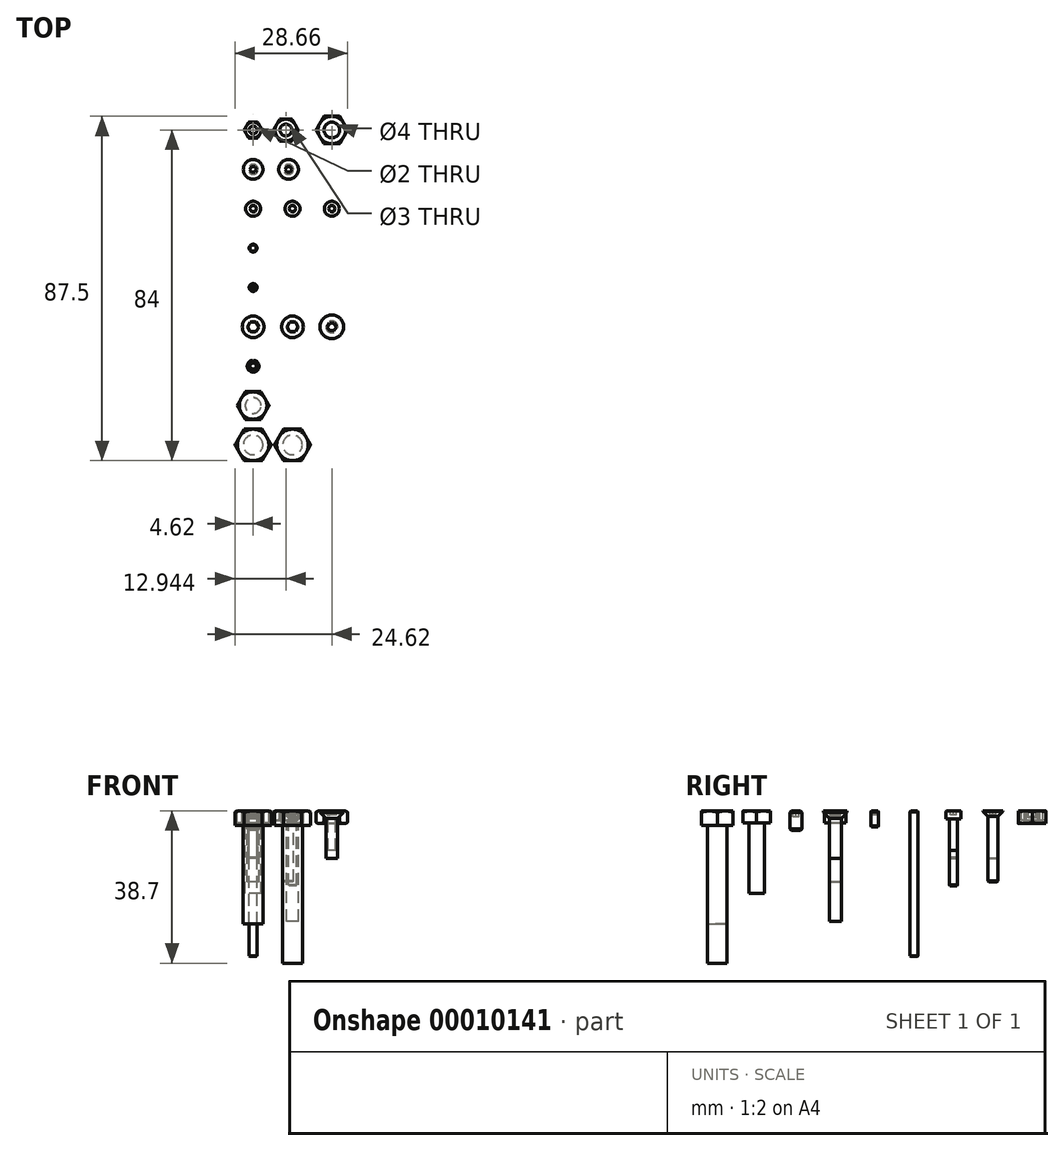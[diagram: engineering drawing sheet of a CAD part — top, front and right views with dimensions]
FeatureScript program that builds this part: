
annotation { "Feature Type Name" : "Feature", "Feature Type Description" : "" }
export const myFeature = defineFeature(function(context is Context, id is Id, definition is map)
    precondition{}
    {
        {
            var Q0;
            Q0=qCreatedBy(makeId("Top.planeOp"),FACE);
            var sketch = newSketch(context, id + "F0", { "sketchPlane" : qUnion([Q0])});
            skCircle(sketch, "E0.cCircle", {"center": v(0, 0) * mm, "radius": 2 * mm, "construction": true});
            skLineSegment(sketch, "E0.0", {"start": v(1.15, -2) * mm, "end": v(-1.15, -2) * mm});
            skLineSegment(sketch, "E0.1", {"start": v(-1.15, -2) * mm, "end": v(-2.3, 0) * mm});
            skLineSegment(sketch, "E0.2", {"start": v(-2.3, 0) * mm, "end": v(-1.15, 2) * mm});
            skLineSegment(sketch, "E0.3", {"start": v(-1.15, 2) * mm, "end": v(1.15, 2) * mm});
            skLineSegment(sketch, "E0.4", {"start": v(1.15, 2) * mm, "end": v(2.3, 0) * mm});
            skLineSegment(sketch, "E0.5", {"start": v(2.3, 0) * mm, "end": v(1.15, -2) * mm});
            skPoint(sketch, "E0.0.midPoint", {"position": v(0, -2) * mm});
            skCircle(sketch, "E1", {"center": v(0, 0) * mm, "radius": 1 * mm});
            skCircle(sketch, "E2", {"center": v(0, 0) * mm, "radius": 2 * mm});
            skSolve(sketch);
        }
        {
            var Q0;
            {var subQ1=sQuery(id+"F0.wireOp",EDGE,"E0.3");var subQ3=sQuery(id+"F0.wireOp",EDGE,"E0.2");var subQ5=makeQuery(id+"F0.imprint","INTERSECT",VERTEX,{"derivedFrom":[subQ3,subQ1]});Q0=makeQuery(id+"F0.imprint","IMPRINT",FACE,{"disambiguationData":[TD([[makeQuery(id+"F0.imprint","IMPRINT",EDGE,{"disambiguationData":[TD([[subQ5,1.0]])],"derivedFrom":subQ3}),-1.0]])]});}
            var Q1;
            {var subQ1=sQuery(id+"F0.wireOp",EDGE,"E0.2");var subQ3=sQuery(id+"F0.wireOp",EDGE,"E0.1");var subQ5=makeQuery(id+"F0.imprint","INTERSECT",VERTEX,{"derivedFrom":[subQ3,subQ1]});Q1=makeQuery(id+"F0.imprint","IMPRINT",FACE,{"disambiguationData":[TD([[makeQuery(id+"F0.imprint","IMPRINT",EDGE,{"disambiguationData":[TD([[subQ5,1.0]])],"derivedFrom":subQ3}),-1.0]])]});}
            var Q2;
            Q2=makeQuery(id+"F0.imprint","IMPRINT",FACE,{"disambiguationData":[TD([[makeQuery(id+"F0.imprint","IMPRINT",EDGE,{"derivedFrom":sQuery(id+"F0.wireOp",EDGE,"E1")}),-1.0]])]});
            var Q3;
            {var subQ1=sQuery(id+"F0.wireOp",EDGE,"E0.4");var subQ3=sQuery(id+"F0.wireOp",EDGE,"E0.3");var subQ5=makeQuery(id+"F0.imprint","INTERSECT",VERTEX,{"derivedFrom":[subQ3,subQ1]});Q3=makeQuery(id+"F0.imprint","IMPRINT",FACE,{"disambiguationData":[TD([[makeQuery(id+"F0.imprint","IMPRINT",EDGE,{"disambiguationData":[TD([[subQ5,1.0]])],"derivedFrom":subQ3}),-1.0]])]});}
            var Q4;
            {var subQ1=sQuery(id+"F0.wireOp",EDGE,"E0.5");var subQ3=sQuery(id+"F0.wireOp",EDGE,"E0.4");var subQ5=makeQuery(id+"F0.imprint","INTERSECT",VERTEX,{"derivedFrom":[subQ3,subQ1]});Q4=makeQuery(id+"F0.imprint","IMPRINT",FACE,{"disambiguationData":[TD([[makeQuery(id+"F0.imprint","IMPRINT",EDGE,{"disambiguationData":[TD([[subQ5,1.0]])],"derivedFrom":subQ3}),-1.0]])]});}
            var Q5;
            {var subQ1=sQuery(id+"F0.wireOp",EDGE,"E0.5");var subQ3=sQuery(id+"F0.wireOp",EDGE,"E0.0");var subQ5=makeQuery(id+"F0.imprint","INTERSECT",VERTEX,{"derivedFrom":[subQ3,subQ1]});Q5=makeQuery(id+"F0.imprint","IMPRINT",FACE,{"disambiguationData":[TD([[makeQuery(id+"F0.imprint","IMPRINT",EDGE,{"disambiguationData":[TD([[subQ5,-1.0]])],"derivedFrom":subQ3}),-1.0]])]});}
            var Q6;
            {var subQ1=sQuery(id+"F0.wireOp",EDGE,"E0.1");var subQ3=sQuery(id+"F0.wireOp",EDGE,"E0.0");var subQ5=makeQuery(id+"F0.imprint","INTERSECT",VERTEX,{"derivedFrom":[subQ3,subQ1]});Q6=makeQuery(id+"F0.imprint","IMPRINT",FACE,{"disambiguationData":[TD([[makeQuery(id+"F0.imprint","IMPRINT",EDGE,{"disambiguationData":[TD([[subQ5,1.0]])],"derivedFrom":subQ3}),-1.0]])]});}
            extrude(context, id + "F1", {"entities" : qUnion([Q0, Q1, Q2, Q3, Q4, Q5, Q6]), "oppositeDirection" : true, "depth" : 1.6 * mm});
        }
        {
            var Q0;
            Q0=qCreatedBy(makeId("Front.planeOp"),FACE);
            var sketch = newSketch(context, id + "F2", { "sketchPlane" : qUnion([Q0])});
            skLineSegment(sketch, "E3.0", {"start": v(-2, 0) * mm, "end": v(2, 0) * mm});
            skLineSegment(sketch, "E3.1", {"start": v(2.3, -1.6) * mm, "end": v(2.3, 0) * mm});
            skLineSegment(sketch, "E3.2", {"start": v(-2.3, -1.6) * mm, "end": v(-2.3, 0) * mm});
            skLineSegment(sketch, "E4", {"start": v(2, 0) * mm, "end": v(2.3, -0.18) * mm});
            skLineSegment(sketch, "E5", {"start": v(2, 0) * mm, "end": v(2.3, 0) * mm});
            skLineSegment(sketch, "E6", {"start": v(0, 0) * mm, "end": v(0, -1.88) * mm, "construction": true});
            skLineSegment(sketch, "E7", {"start": v(-2.3, -0.8) * mm, "end": v(0, -0.8) * mm, "construction": true});
            skLineSegment(sketch, "E8.0.MirrorCS", {"start": v(2, -1.6) * mm, "end": v(2.3, -1.6) * mm});
            skLineSegment(sketch, "E9.0.MirrorCS", {"start": v(2.3, 0) * mm, "end": v(2.3, -1.6) * mm});
            skLineSegment(sketch, "E10.0.MirrorCS", {"start": v(2, -1.6) * mm, "end": v(2.3, -1.42) * mm});
            skSolve(sketch);
        }
        {
            var Q0;
            {var subQ2=sQuery(id+"F2.wireOp",EDGE,"E4");Q0=makeQuery(id+"F2.imprint","IMPRINT",FACE,{"disambiguationData":[TD([[makeQuery(id+"F2.imprint","IMPRINT",EDGE,{"derivedFrom":subQ2}),1.0]])]});}
            var Q1;
            {var subQ2=sQuery(id+"F2.wireOp",EDGE,"E8.0.MirrorCS");Q1=makeQuery(id+"F2.imprint","IMPRINT",FACE,{"disambiguationData":[TD([[makeQuery(id+"F2.imprint","IMPRINT",EDGE,{"derivedFrom":subQ2}),1.0]])]});}
            var Q2;
            Q2=sQuery(id+"F2.wireOp",EDGE,"E6");
            revolve(context, id + "F3", {"operationType" : NewBodyOperationType.REMOVE, "entities" : qUnion([Q0, Q1]), "axis" : qUnion([Q2]), "revolveType" : RevolveType.FULL, "oppositeDirection" : true});
        }
        {
            var Q0;
            Q0=qCreatedBy(makeId("Top.planeOp"),FACE);
            var sketch = newSketch(context, id + "F4", { "sketchPlane" : qUnion([Q0])});
            skCircle(sketch, "E11.cCircle", {"center": v(8.32, 0) * mm, "radius": 2.75 * mm, "construction": true});
            skLineSegment(sketch, "E11.0", {"start": v(9.91, -2.75) * mm, "end": v(6.74, -2.75) * mm});
            skLineSegment(sketch, "E11.1", {"start": v(6.74, -2.75) * mm, "end": v(5.15, 0) * mm});
            skLineSegment(sketch, "E11.2", {"start": v(5.15, 0) * mm, "end": v(6.74, 2.75) * mm});
            skLineSegment(sketch, "E11.3", {"start": v(6.74, 2.75) * mm, "end": v(9.91, 2.75) * mm});
            skLineSegment(sketch, "E11.4", {"start": v(9.91, 2.75) * mm, "end": v(11.5, 0) * mm});
            skLineSegment(sketch, "E11.5", {"start": v(11.5, 0) * mm, "end": v(9.91, -2.75) * mm});
            skPoint(sketch, "E11.0.midPoint", {"position": v(8.32, -2.75) * mm});
            skCircle(sketch, "E12", {"center": v(8.32, 0) * mm, "radius": 1.5 * mm});
            skSolve(sketch);
        }
        {
            var Q0;
            Q0=makeQuery(id+"F4.imprint","IMPRINT",FACE,{"disambiguationData":[TD([[makeQuery(id+"F4.imprint","IMPRINT",EDGE,{"derivedFrom":sQuery(id+"F4.wireOp",EDGE,"E11.0")}),-1.0]])]});
            extrude(context, id + "F5", {"entities" : qUnion([Q0]), "oppositeDirection" : true, "depth" : 2.4 * mm});
        }
        {
            var Q0;
            Q0=qCreatedBy(makeId("Front.planeOp"),FACE);
            var sketch = newSketch(context, id + "F6", { "sketchPlane" : qUnion([Q0])});
            skLineSegment(sketch, "E13.0", {"start": v(5.57, 0) * mm, "end": v(11.07, 0) * mm});
            skLineSegment(sketch, "E13.1", {"start": v(5.15, -2.4) * mm, "end": v(5.15, 0) * mm});
            skLineSegment(sketch, "E13.2", {"start": v(11.5, -2.4) * mm, "end": v(11.5, 0) * mm});
            skLineSegment(sketch, "E14", {"start": v(5.57, 0) * mm, "end": v(5.15, -0.25) * mm});
            skLineSegment(sketch, "E15", {"start": v(5.57, 0) * mm, "end": v(5.15, 0) * mm});
            skLineSegment(sketch, "E16", {"start": v(8.32, 0) * mm, "end": v(8.32, -2.47) * mm, "construction": true});
            skLineSegment(sketch, "E17", {"start": v(11.5, -1.2) * mm, "end": v(8.32, -1.2) * mm, "construction": true});
            skLineSegment(sketch, "E18.0.MirrorCS", {"start": v(5.57, -2.4) * mm, "end": v(5.15, -2.15) * mm});
            skLineSegment(sketch, "E19.0.MirrorCS", {"start": v(5.15, 0) * mm, "end": v(5.15, -2.4) * mm});
            skLineSegment(sketch, "E20.0.MirrorCS", {"start": v(5.57, -2.4) * mm, "end": v(5.15, -2.4) * mm});
            skSolve(sketch);
        }
        {
            var Q0;
            {var subQ2=sQuery(id+"F6.wireOp",EDGE,"E14");Q0=makeQuery(id+"F6.imprint","IMPRINT",FACE,{"disambiguationData":[TD([[makeQuery(id+"F6.imprint","IMPRINT",EDGE,{"derivedFrom":subQ2}),-1.0]])]});}
            var Q1;
            {var subQ2=sQuery(id+"F6.wireOp",EDGE,"E18.0.MirrorCS");Q1=makeQuery(id+"F6.imprint","IMPRINT",FACE,{"disambiguationData":[TD([[makeQuery(id+"F6.imprint","IMPRINT",EDGE,{"derivedFrom":subQ2}),1.0]])]});}
            var Q2;
            Q2=sQuery(id+"F6.wireOp",EDGE,"E16");
            revolve(context, id + "F7", {"operationType" : NewBodyOperationType.REMOVE, "entities" : qUnion([Q0, Q1]), "axis" : qUnion([Q2]), "revolveType" : RevolveType.FULL, "oppositeDirection" : true});
        }
        {
            var Q0;
            Q0=qCreatedBy(makeId("Top.planeOp"),FACE);
            var sketch = newSketch(context, id + "F8", { "sketchPlane" : qUnion([Q0])});
            skCircle(sketch, "E21", {"center": v(17, 0) * mm, "radius": 2.5 * mm});
            skCircle(sketch, "E22", {"center": v(17, 0) * mm, "radius": 1.25 * mm});
            skCircle(sketch, "E23.cCircle", {"center": v(17, 0) * mm, "radius": 0.75 * mm, "construction": true});
            skLineSegment(sketch, "E23.0", {"start": v(17.43, -0.75) * mm, "end": v(16.57, -0.75) * mm});
            skLineSegment(sketch, "E23.1", {"start": v(16.57, -0.75) * mm, "end": v(16.13, 0) * mm});
            skLineSegment(sketch, "E23.2", {"start": v(16.13, 0) * mm, "end": v(16.57, 0.75) * mm});
            skLineSegment(sketch, "E23.3", {"start": v(16.57, 0.75) * mm, "end": v(17.43, 0.75) * mm});
            skLineSegment(sketch, "E23.4", {"start": v(17.43, 0.75) * mm, "end": v(17.87, 0) * mm});
            skLineSegment(sketch, "E23.5", {"start": v(17.87, 0) * mm, "end": v(17.43, -0.75) * mm});
            skPoint(sketch, "E23.0.midPoint", {"position": v(17, -0.75) * mm});
            skSolve(sketch);
        }
        {
            var Q0;
            Q0=makeQuery(id+"F8.imprint","IMPRINT",FACE,{"disambiguationData":[TD([[makeQuery(id+"F8.imprint","IMPRINT",EDGE,{"derivedFrom":sQuery(id+"F8.wireOp",EDGE,"E22")}),1.0]])]});
            var Q1;
            Q1=makeQuery(id+"F8.imprint","IMPRINT",FACE,{"disambiguationData":[TD([[makeQuery(id+"F8.imprint","IMPRINT",EDGE,{"derivedFrom":sQuery(id+"F8.wireOp",EDGE,"E23.0")}),-1.0]])]});
            extrude(context, id + "F9", {"entities" : qUnion([Q0, Q1]), "oppositeDirection" : true, "depth" : 15 * mm});
        }
        {
            var Q0;
            Q0=makeQuery(id+"F8.imprint","IMPRINT",FACE,{"disambiguationData":[TD([[makeQuery(id+"F8.imprint","IMPRINT",EDGE,{"derivedFrom":sQuery(id+"F8.wireOp",EDGE,"E21")}),1.0]])]});
            extrude(context, id + "F10", {"entities" : qUnion([Q0]), "operationType" : NewBodyOperationType.ADD, "oppositeDirection" : true, "depth" : 1.5 * mm});
        }
        {
            var Q0;
            Q0=makeQuery(id+"F10.opExtrude","CAP_EDGE",EDGE,{"disambiguationData":[OSD([sQuery(id+"F8.wireOp",EDGE,"E21")])],"isStart":false});
            chamfer(context, id + "F11", {"entities" : qUnion([Q0]), "width" : 1.4 * mm, "tangentPropagation" : true});
        }
        {
            var Q0;
            Q0=makeQuery(id+"F8.imprint","IMPRINT",FACE,{"disambiguationData":[TD([[makeQuery(id+"F8.imprint","IMPRINT",EDGE,{"derivedFrom":sQuery(id+"F8.wireOp",EDGE,"E23.0")}),-1.0]])]});
            extrude(context, id + "F12", {"entities" : qUnion([Q0]), "operationType" : NewBodyOperationType.REMOVE, "oppositeDirection" : true, "depth" : 1 * mm});
        }
        {
            var Q0;
            Q0=makeQuery(id+"F9.opExtrude","SWEPT_BODY",BODY,{"disambiguationData":[OSD([sQuery(id+"F8.wireOp",EDGE,"E22")])]});
            transform(context, id + "F13", {"entities" : qUnion([Q0]), "transformType" : TransformType.TRANSLATION_3D, "dx" : 10 * mm, "dy" : 0 * mm, "dz" : 0 * mm, "makeCopy" : true});
        }
        {
            var Q0;
            Q0=makeQuery(id+"F13.opPattern","COPY",FACE,{"derivedFrom":makeQuery(id+"F9.opExtrude","CAP_FACE",FACE,{"disambiguationData":[OSD([sQuery(id+"F8.wireOp",EDGE,"E22")])],"isStart":false}),"instanceName":"1"});
            extrude(context, id + "F14", {"entities" : qUnion([Q0]), "operationType" : NewBodyOperationType.ADD, "depth" : 3 * mm});
        }
        {
            var Q0;
            Q0=makeQuery(id+"F9.opExtrude","SWEPT_BODY",BODY,{"disambiguationData":[OSD([sQuery(id+"F8.wireOp",EDGE,"E22")])]});
            transform(context, id + "F15", {"entities" : qUnion([Q0]), "transformType" : TransformType.TRANSLATION_3D, "dx" : -(17 * mm), "dy" : -(10 * mm), "dz" : 0 * mm, "makeCopy" : false});
        }
        {
            var Q0;
            Q0=makeQuery(id+"F13.opPattern","COPY",BODY,{"derivedFrom":makeQuery(id+"F9.opExtrude","SWEPT_BODY",BODY,{"disambiguationData":[OSD([sQuery(id+"F8.wireOp",EDGE,"E22")])]}),"instanceName":"1"});
            transform(context, id + "F16", {"entities" : qUnion([Q0]), "transformType" : TransformType.TRANSLATION_3D, "dx" : -(18 * mm), "dy" : -10 * mm, "dz" : 0 * mm, "makeCopy" : false});
        }
        {
            var Q0;
            Q0=qCreatedBy(makeId("Top.planeOp"),FACE);
            var sketch = newSketch(context, id + "F17", { "sketchPlane" : qUnion([Q0])});
            skCircle(sketch, "E24", {"center": v(0, -20) * mm, "radius": 1.9 * mm});
            skCircle(sketch, "E25", {"center": v(0, -20) * mm, "radius": 1 * mm});
            skCircle(sketch, "E26.cCircle", {"center": v(0, -20) * mm, "radius": 0.75 * mm, "construction": true});
            skLineSegment(sketch, "E26.0", {"start": v(0.43, -20.75) * mm, "end": v(-0.43, -20.75) * mm});
            skLineSegment(sketch, "E26.1", {"start": v(-0.43, -20.75) * mm, "end": v(-0.87, -20) * mm});
            skLineSegment(sketch, "E26.2", {"start": v(-0.87, -20) * mm, "end": v(-0.43, -19.25) * mm});
            skLineSegment(sketch, "E26.3", {"start": v(-0.43, -19.25) * mm, "end": v(0.43, -19.25) * mm});
            skLineSegment(sketch, "E26.4", {"start": v(0.43, -19.25) * mm, "end": v(0.87, -20) * mm});
            skLineSegment(sketch, "E26.5", {"start": v(0.87, -20) * mm, "end": v(0.43, -20.75) * mm});
            skPoint(sketch, "E26.0.midPoint", {"position": v(0, -20.75) * mm});
            skSolve(sketch);
        }
        {
            var Q0;
            Q0=makeQuery(id+"F17.imprint","IMPRINT",FACE,{"disambiguationData":[TD([[makeQuery(id+"F17.imprint","IMPRINT",EDGE,{"derivedFrom":sQuery(id+"F17.wireOp",EDGE,"E25")}),1.0]])]});
            var Q1;
            Q1=makeQuery(id+"F17.imprint","IMPRINT",FACE,{"disambiguationData":[TD([[makeQuery(id+"F17.imprint","IMPRINT",EDGE,{"derivedFrom":sQuery(id+"F17.wireOp",EDGE,"E26.0")}),-1.0]])]});
            extrude(context, id + "F18", {"entities" : qUnion([Q0, Q1]), "oppositeDirection" : true, "depth" : 12 * mm});
        }
        {
            var Q0;
            Q0=makeQuery(id+"F17.imprint","IMPRINT",FACE,{"disambiguationData":[TD([[makeQuery(id+"F17.imprint","IMPRINT",EDGE,{"derivedFrom":sQuery(id+"F17.wireOp",EDGE,"E24")}),1.0]])]});
            extrude(context, id + "F19", {"entities" : qUnion([Q0]), "operationType" : NewBodyOperationType.ADD, "oppositeDirection" : true, "depth" : 2 * mm});
        }
        {
            var Q0;
            Q0=makeQuery(id+"F17.imprint","IMPRINT",FACE,{"disambiguationData":[TD([[makeQuery(id+"F17.imprint","IMPRINT",EDGE,{"derivedFrom":sQuery(id+"F17.wireOp",EDGE,"E26.0")}),-1.0]])]});
            extrude(context, id + "F20", {"entities" : qUnion([Q0]), "operationType" : NewBodyOperationType.REMOVE, "oppositeDirection" : true, "depth" : 1 * mm});
        }
        {
            var Q0;
            Q0=makeQuery(id+"F19.opExtrude","CAP_EDGE",EDGE,{"disambiguationData":[OSD([sQuery(id+"F17.wireOp",EDGE,"E24")])],"isStart":true});
            fillet(context, id + "F21", {"entities" : qUnion([Q0]), "radius" : 0.2 * mm, "tangentPropagation" : true, "allowEdgeOverflow" : false});
        }
        {
            var Q0;
            Q0=makeQuery(id+"F18.opExtrude","SWEPT_BODY",BODY,{"disambiguationData":[OSD([sQuery(id+"F17.wireOp",EDGE,"E25")])]});
            transform(context, id + "F22", {"entities" : qUnion([Q0]), "transformType" : TransformType.TRANSLATION_3D, "dx" : 10 * mm, "dy" : 0 * mm, "dz" : 0 * mm, "makeCopy" : true});
        }
        {
            var Q0;
            Q0=makeQuery(id+"F22.opPattern","COPY",FACE,{"derivedFrom":makeQuery(id+"F18.opExtrude","CAP_FACE",FACE,{"disambiguationData":[OSD([sQuery(id+"F17.wireOp",EDGE,"E25")])],"isStart":false}),"instanceName":"1"});
            extrude(context, id + "F23", {"entities" : qUnion([Q0]), "operationType" : NewBodyOperationType.ADD, "depth" : 7 * mm});
        }
        {
            var Q0;
            Q0=qCreatedBy(makeId("Top.planeOp"),FACE);
            var sketch = newSketch(context, id + "F24", { "sketchPlane" : qUnion([Q0])});
            skCircle(sketch, "E27", {"center": v(0, -30) * mm, "radius": 1 * mm});
            skSolve(sketch);
        }
        {
            var Q0;
            Q0=makeQuery(id+"F24.imprint","IMPRINT",FACE,{"disambiguationData":[TD([[makeQuery(id+"F24.imprint","IMPRINT",EDGE,{"derivedFrom":sQuery(id+"F24.wireOp",EDGE,"E27")}),1.0]])]});
            extrude(context, id + "F25", {"entities" : qUnion([Q0]), "oppositeDirection" : true, "depth" : 37 * mm});
        }
        {
            var Q0;
            Q0=makeQuery(id+"F25.opExtrude","CAP_EDGE",EDGE,{"disambiguationData":[OSD([sQuery(id+"F24.wireOp",EDGE,"E27")])],"isStart":false});
            var Q1;
            Q1=makeQuery(id+"F25.opExtrude","CAP_EDGE",EDGE,{"disambiguationData":[OSD([sQuery(id+"F24.wireOp",EDGE,"E27")])],"isStart":true});
            chamfer(context, id + "F26", {"entities" : qUnion([Q0, Q1]), "width" : 0.2 * mm, "tangentPropagation" : true});
        }
        {
            var Q0;
            Q0=makeQuery(id+"F22.opPattern","COPY",BODY,{"derivedFrom":makeQuery(id+"F18.opExtrude","SWEPT_BODY",BODY,{"disambiguationData":[OSD([sQuery(id+"F17.wireOp",EDGE,"E25")])]}),"instanceName":"1"});
            transform(context, id + "F27", {"entities" : qUnion([Q0]), "transformType" : TransformType.TRANSLATION_3D, "dx" : 10 * mm, "dy" : 0 * mm, "dz" : 0 * mm, "makeCopy" : true});
        }
        {
            var Q0;
            Q0=makeQuery(id+"F27.opPattern","COPY",FACE,{"derivedFrom":makeQuery(id+"F23.opExtrude","CAP_FACE",FACE,{"disambiguationData":[OSD([sQuery(id+"F17.wireOp",EDGE,"E25")])],"isStart":false}),"instanceName":"1"});
            extrude(context, id + "F28", {"entities" : qUnion([Q0]), "operationType" : NewBodyOperationType.REMOVE, "oppositeDirection" : true, "depth" : 9 * mm});
        }
        {
            var Q0;
            Q0=qCreatedBy(makeId("Top.planeOp"),FACE);
            var sketch = newSketch(context, id + "F29", { "sketchPlane" : qUnion([Q0])});
            skCircle(sketch, "E28", {"center": v(0, -40) * mm, "radius": 1 * mm});
            skCircle(sketch, "E29.cCircle", {"center": v(0, -40) * mm, "radius": 0.45 * mm, "construction": true});
            skLineSegment(sketch, "E29.0", {"start": v(0.26, -40.45) * mm, "end": v(-0.26, -40.45) * mm});
            skLineSegment(sketch, "E29.1", {"start": v(-0.26, -40.45) * mm, "end": v(-0.52, -40) * mm});
            skLineSegment(sketch, "E29.2", {"start": v(-0.52, -40) * mm, "end": v(-0.26, -39.55) * mm});
            skLineSegment(sketch, "E29.3", {"start": v(-0.26, -39.55) * mm, "end": v(0.26, -39.55) * mm});
            skLineSegment(sketch, "E29.4", {"start": v(0.26, -39.55) * mm, "end": v(0.52, -40) * mm});
            skLineSegment(sketch, "E29.5", {"start": v(0.52, -40) * mm, "end": v(0.26, -40.45) * mm});
            skPoint(sketch, "E29.0.midPoint", {"position": v(0, -40.45) * mm});
            skSolve(sketch);
        }
        {
            var Q0;
            Q0=makeQuery(id+"F29.imprint","IMPRINT",FACE,{"disambiguationData":[TD([[makeQuery(id+"F29.imprint","IMPRINT",EDGE,{"derivedFrom":sQuery(id+"F29.wireOp",EDGE,"E28")}),1.0]])]});
            var Q1;
            Q1=makeQuery(id+"F29.imprint","IMPRINT",FACE,{"disambiguationData":[TD([[makeQuery(id+"F29.imprint","IMPRINT",EDGE,{"derivedFrom":sQuery(id+"F29.wireOp",EDGE,"E29.0")}),-1.0]])]});
            extrude(context, id + "F30", {"entities" : qUnion([Q0, Q1]), "oppositeDirection" : true, "depth" : 4 * mm});
        }
        {
            var Q0;
            Q0=makeQuery(id+"F29.imprint","IMPRINT",FACE,{"disambiguationData":[TD([[makeQuery(id+"F29.imprint","IMPRINT",EDGE,{"derivedFrom":sQuery(id+"F29.wireOp",EDGE,"E29.0")}),-1.0]])]});
            extrude(context, id + "F31", {"entities" : qUnion([Q0]), "operationType" : NewBodyOperationType.REMOVE, "oppositeDirection" : true, "depth" : 1 * mm});
        }
        {
            var Q0;
            Q0=makeQuery(id+"F30.opExtrude","CAP_EDGE",EDGE,{"disambiguationData":[OSD([sQuery(id+"F29.wireOp",EDGE,"E28")])],"isStart":true});
            var Q1;
            Q1=makeQuery(id+"F30.opExtrude","CAP_EDGE",EDGE,{"disambiguationData":[OSD([sQuery(id+"F29.wireOp",EDGE,"E28")])],"isStart":false});
            chamfer(context, id + "F32", {"entities" : qUnion([Q0, Q1]), "width" : 0.2 * mm, "tangentPropagation" : true});
        }
        {
            var Q0;
            Q0=qCreatedBy(makeId("Top.planeOp"),FACE);
            var sketch = newSketch(context, id + "F33", { "sketchPlane" : qUnion([Q0])});
            skCircle(sketch, "E30", {"center": v(0, -50) * mm, "radius": 1.5 * mm});
            skCircle(sketch, "E31", {"center": v(0, -50) * mm, "radius": 2.75 * mm});
            skCircle(sketch, "E32.cCircle", {"center": v(0, -50) * mm, "radius": 1.25 * mm, "construction": true});
            skLineSegment(sketch, "E32.0", {"start": v(0.72, -51.25) * mm, "end": v(-0.72, -51.25) * mm});
            skLineSegment(sketch, "E32.1", {"start": v(-0.72, -51.25) * mm, "end": v(-1.44, -50) * mm});
            skLineSegment(sketch, "E32.2", {"start": v(-1.44, -50) * mm, "end": v(-0.72, -48.75) * mm});
            skLineSegment(sketch, "E32.3", {"start": v(-0.72, -48.75) * mm, "end": v(0.72, -48.75) * mm});
            skLineSegment(sketch, "E32.4", {"start": v(0.72, -48.75) * mm, "end": v(1.44, -50) * mm});
            skLineSegment(sketch, "E32.5", {"start": v(1.44, -50) * mm, "end": v(0.72, -51.25) * mm});
            skPoint(sketch, "E32.0.midPoint", {"position": v(0, -51.25) * mm});
            skSolve(sketch);
        }
        {
            var Q0;
            Q0=makeQuery(id+"F33.imprint","IMPRINT",FACE,{"disambiguationData":[TD([[makeQuery(id+"F33.imprint","IMPRINT",EDGE,{"derivedFrom":sQuery(id+"F33.wireOp",EDGE,"E32.0")}),-1.0]])]});
            var Q1;
            Q1=makeQuery(id+"F33.imprint","IMPRINT",FACE,{"disambiguationData":[TD([[makeQuery(id+"F33.imprint","IMPRINT",EDGE,{"derivedFrom":sQuery(id+"F33.wireOp",EDGE,"E30")}),1.0]])]});
            extrude(context, id + "F34", {"entities" : qUnion([Q0, Q1]), "oppositeDirection" : true, "depth" : 18 * mm});
        }
        {
            var Q0;
            Q0=makeQuery(id+"F33.imprint","IMPRINT",FACE,{"disambiguationData":[TD([[makeQuery(id+"F33.imprint","IMPRINT",EDGE,{"derivedFrom":sQuery(id+"F33.wireOp",EDGE,"E30")}),-1.0]])]});
            extrude(context, id + "F35", {"entities" : qUnion([Q0]), "operationType" : NewBodyOperationType.ADD, "oppositeDirection" : true, "depth" : 3 * mm});
        }
        {
            var Q0;
            Q0=makeQuery(id+"F33.imprint","IMPRINT",FACE,{"disambiguationData":[TD([[makeQuery(id+"F33.imprint","IMPRINT",EDGE,{"derivedFrom":sQuery(id+"F33.wireOp",EDGE,"E32.0")}),-1.0]])]});
            extrude(context, id + "F36", {"entities" : qUnion([Q0]), "operationType" : NewBodyOperationType.REMOVE, "oppositeDirection" : true, "depth" : 1.5 * mm});
        }
        {
            var Q0;
            Q0=makeQuery(id+"F35.opExtrude","CAP_EDGE",EDGE,{"disambiguationData":[OSD([sQuery(id+"F33.wireOp",EDGE,"E31")])],"isStart":true});
            fillet(context, id + "F37", {"entities" : qUnion([Q0]), "radius" : 0.2 * mm, "tangentPropagation" : true, "allowEdgeOverflow" : false});
        }
        {
            var Q0;
            Q0=qCreatedBy(makeId("Top.planeOp"),FACE);
            var sketch = newSketch(context, id + "F38", { "sketchPlane" : qUnion([Q0])});
            skCircle(sketch, "E33", {"center": v(0, -60) * mm, "radius": 1.5 * mm});
            skCircle(sketch, "E34.cCircle", {"center": v(0, -60) * mm, "radius": 0.75 * mm, "construction": true});
            skLineSegment(sketch, "E34.0", {"start": v(0.43, -60.75) * mm, "end": v(-0.43, -60.75) * mm});
            skLineSegment(sketch, "E34.1", {"start": v(-0.43, -60.75) * mm, "end": v(-0.87, -60) * mm});
            skLineSegment(sketch, "E34.2", {"start": v(-0.87, -60) * mm, "end": v(-0.43, -59.25) * mm});
            skLineSegment(sketch, "E34.3", {"start": v(-0.43, -59.25) * mm, "end": v(0.43, -59.25) * mm});
            skLineSegment(sketch, "E34.4", {"start": v(0.43, -59.25) * mm, "end": v(0.87, -60) * mm});
            skLineSegment(sketch, "E34.5", {"start": v(0.87, -60) * mm, "end": v(0.43, -60.75) * mm});
            skPoint(sketch, "E34.0.midPoint", {"position": v(0, -60.75) * mm});
            skSolve(sketch);
        }
        {
            var Q0;
            Q0=makeQuery(id+"F38.imprint","IMPRINT",FACE,{"disambiguationData":[TD([[makeQuery(id+"F38.imprint","IMPRINT",EDGE,{"derivedFrom":sQuery(id+"F38.wireOp",EDGE,"E33")}),1.0]])]});
            var Q1;
            Q1=makeQuery(id+"F38.imprint","IMPRINT",FACE,{"disambiguationData":[TD([[makeQuery(id+"F38.imprint","IMPRINT",EDGE,{"derivedFrom":sQuery(id+"F38.wireOp",EDGE,"E34.0")}),-1.0]])]});
            extrude(context, id + "F39", {"entities" : qUnion([Q0, Q1]), "oppositeDirection" : true, "depth" : 5 * mm});
        }
        {
            var Q0;
            Q0=makeQuery(id+"F38.imprint","IMPRINT",FACE,{"disambiguationData":[TD([[makeQuery(id+"F38.imprint","IMPRINT",EDGE,{"derivedFrom":sQuery(id+"F38.wireOp",EDGE,"E34.0")}),-1.0]])]});
            extrude(context, id + "F40", {"entities" : qUnion([Q0]), "operationType" : NewBodyOperationType.REMOVE, "oppositeDirection" : true, "depth" : 1.5 * mm});
        }
        {
            var Q0;
            Q0=makeQuery(id+"F39.opExtrude","CAP_EDGE",EDGE,{"disambiguationData":[OSD([sQuery(id+"F38.wireOp",EDGE,"E33")])],"isStart":true});
            var Q1;
            Q1=makeQuery(id+"F39.opExtrude","CAP_EDGE",EDGE,{"disambiguationData":[OSD([sQuery(id+"F38.wireOp",EDGE,"E33")])],"isStart":false});
            chamfer(context, id + "F41", {"entities" : qUnion([Q0, Q1]), "width" : 0.4 * mm, "tangentPropagation" : true});
        }
        {
            var Q0;
            Q0=makeQuery(id+"F9.opExtrude","CAP_FACE",FACE,{"disambiguationData":[OSD([sQuery(id+"F8.wireOp",EDGE,"E22")])],"isStart":false});
            extrude(context, id + "F42", {"entities" : qUnion([Q0]), "operationType" : NewBodyOperationType.REMOVE, "oppositeDirection" : true, "depth" : 3 * mm});
        }
        {
            var Q0;
            Q0=makeQuery(id+"F18.opExtrude","CAP_EDGE",EDGE,{"disambiguationData":[OSD([sQuery(id+"F17.wireOp",EDGE,"E25")])],"isStart":false});
            var Q1;
            Q1=makeQuery(id+"F23.opExtrude","CAP_EDGE",EDGE,{"disambiguationData":[OSD([sQuery(id+"F17.wireOp",EDGE,"E25")])],"isStart":false});
            var Q2;
            Q2=makeQuery(id+"F28.boolean.opBoolean","COPY",EDGE,{"derivedFrom":makeQuery(id+"F28.opExtrude","CAP_EDGE",EDGE,{"disambiguationData":[OSD([sQuery(id+"F17.wireOp",EDGE,"E25")])],"isStart":false})});
            chamfer(context, id + "F43", {"entities" : qUnion([Q0, Q1, Q2]), "width" : 0.15 * mm, "tangentPropagation" : true});
        }
        {
            var Q0;
            Q0=makeQuery(id+"F42.boolean.opBoolean","COPY",EDGE,{"derivedFrom":makeQuery(id+"F42.opExtrude","CAP_EDGE",EDGE,{"disambiguationData":[OSD([sQuery(id+"F8.wireOp",EDGE,"E22")])],"isStart":false})});
            var Q1;
            Q1=makeQuery(id+"F14.opExtrude","CAP_EDGE",EDGE,{"disambiguationData":[OSD([sQuery(id+"F8.wireOp",EDGE,"E22")])],"isStart":false});
            chamfer(context, id + "F44", {"entities" : qUnion([Q0, Q1]), "width" : 0.2 * mm, "tangentPropagation" : true});
        }
        {
            var Q0;
            Q0=makeQuery(id+"F34.opExtrude","SWEPT_BODY",BODY,{"disambiguationData":[OSD([sQuery(id+"F33.wireOp",EDGE,"E30")])]});
            transform(context, id + "F45", {"entities" : qUnion([Q0]), "transformType" : TransformType.TRANSLATION_3D, "dx" : 10 * mm, "dy" : 0 * mm, "dz" : 0 * mm, "makeCopy" : true});
        }
        {
            var Q0;
            Q0=makeQuery(id+"F45.opPattern","COPY",FACE,{"derivedFrom":makeQuery(id+"F34.opExtrude","CAP_FACE",FACE,{"disambiguationData":[OSD([sQuery(id+"F33.wireOp",EDGE,"E30")])],"isStart":false}),"instanceName":"1"});
            extrude(context, id + "F46", {"entities" : qUnion([Q0]), "operationType" : NewBodyOperationType.ADD, "depth" : 10 * mm});
        }
        {
            var Q0;
            Q0=qCreatedBy(makeId("Top.planeOp"),FACE);
            var sketch = newSketch(context, id + "F47", { "sketchPlane" : qUnion([Q0])});
            skLineSegment(sketch, "E35", {"start": v(0, 0) * mm, "end": v(20, 0) * mm, "construction": true});
            skCircle(sketch, "E36.cCircle", {"center": v(20, 0) * mm, "radius": 3.5 * mm, "construction": true});
            skLineSegment(sketch, "E36.0", {"start": v(22.02, -3.5) * mm, "end": v(17.98, -3.5) * mm});
            skLineSegment(sketch, "E36.1", {"start": v(17.98, -3.5) * mm, "end": v(15.96, 0) * mm});
            skLineSegment(sketch, "E36.2", {"start": v(15.96, 0) * mm, "end": v(17.98, 3.5) * mm});
            skLineSegment(sketch, "E36.3", {"start": v(17.98, 3.5) * mm, "end": v(22.02, 3.5) * mm});
            skLineSegment(sketch, "E36.4", {"start": v(22.02, 3.5) * mm, "end": v(24.04, 0) * mm});
            skLineSegment(sketch, "E36.5", {"start": v(24.04, 0) * mm, "end": v(22.02, -3.5) * mm});
            skPoint(sketch, "E36.0.midPoint", {"position": v(20, -3.5) * mm});
            skCircle(sketch, "E37", {"center": v(20, 0) * mm, "radius": 2 * mm});
            skCircle(sketch, "E38", {"center": v(20, 0) * mm, "radius": 3.5 * mm});
            skSolve(sketch);
        }
        {
            var Q0;
            {var subQ1=sQuery(id+"F47.wireOp",EDGE,"E36.5");var subQ3=sQuery(id+"F47.wireOp",EDGE,"E36.0");var subQ5=makeQuery(id+"F47.imprint","INTERSECT",VERTEX,{"derivedFrom":[subQ3,subQ1]});var subQ6=sQuery(id+"F47.wireOp",EDGE,"E36.1");var subQ8=makeQuery(id+"F47.imprint","INTERSECT",VERTEX,{"derivedFrom":[subQ3,subQ6]});Q0=qUnion([makeQuery(id+"F47.imprint","IMPRINT",FACE,{"disambiguationData":[TD([[makeQuery(id+"F47.imprint","IMPRINT",EDGE,{"disambiguationData":[TD([[subQ5,-1.0]])],"derivedFrom":subQ3}),-1.0]])]}),makeQuery(id+"F47.imprint","IMPRINT",FACE,{"disambiguationData":[TD([[makeQuery(id+"F47.imprint","IMPRINT",EDGE,{"disambiguationData":[TD([[subQ8,1.0]])],"derivedFrom":subQ3}),-1.0]])]})]);}
            var Q1;
            Q1=makeQuery(id+"F47.imprint","IMPRINT",FACE,{"disambiguationData":[TD([[makeQuery(id+"F47.imprint","IMPRINT",EDGE,{"derivedFrom":sQuery(id+"F47.wireOp",EDGE,"E37")}),-1.0]])]});
            var Q2;
            {var subQ1=sQuery(id+"F47.wireOp",EDGE,"E36.5");var subQ3=sQuery(id+"F47.wireOp",EDGE,"E36.4");var subQ5=makeQuery(id+"F47.imprint","INTERSECT",VERTEX,{"derivedFrom":[subQ3,subQ1]});Q2=makeQuery(id+"F47.imprint","IMPRINT",FACE,{"disambiguationData":[TD([[makeQuery(id+"F47.imprint","IMPRINT",EDGE,{"disambiguationData":[TD([[subQ5,1.0]])],"derivedFrom":subQ3}),-1.0]])]});}
            var Q3;
            {var subQ1=sQuery(id+"F47.wireOp",EDGE,"E36.4");var subQ3=sQuery(id+"F47.wireOp",EDGE,"E36.3");var subQ5=makeQuery(id+"F47.imprint","INTERSECT",VERTEX,{"derivedFrom":[subQ3,subQ1]});Q3=makeQuery(id+"F47.imprint","IMPRINT",FACE,{"disambiguationData":[TD([[makeQuery(id+"F47.imprint","IMPRINT",EDGE,{"disambiguationData":[TD([[subQ5,1.0]])],"derivedFrom":subQ3}),-1.0]])]});}
            var Q4;
            {var subQ1=sQuery(id+"F47.wireOp",EDGE,"E36.3");var subQ3=sQuery(id+"F47.wireOp",EDGE,"E36.2");var subQ5=makeQuery(id+"F47.imprint","INTERSECT",VERTEX,{"derivedFrom":[subQ3,subQ1]});Q4=makeQuery(id+"F47.imprint","IMPRINT",FACE,{"disambiguationData":[TD([[makeQuery(id+"F47.imprint","IMPRINT",EDGE,{"disambiguationData":[TD([[subQ5,1.0]])],"derivedFrom":subQ3}),-1.0]])]});}
            var Q5;
            {var subQ1=sQuery(id+"F47.wireOp",EDGE,"E36.2");var subQ3=sQuery(id+"F47.wireOp",EDGE,"E36.1");var subQ5=makeQuery(id+"F47.imprint","INTERSECT",VERTEX,{"derivedFrom":[subQ3,subQ1]});Q5=makeQuery(id+"F47.imprint","IMPRINT",FACE,{"disambiguationData":[TD([[makeQuery(id+"F47.imprint","IMPRINT",EDGE,{"disambiguationData":[TD([[subQ5,1.0]])],"derivedFrom":subQ3}),-1.0]])]});}
            extrude(context, id + "F48", {"entities" : qUnion([Q0, Q1, Q2, Q3, Q4, Q5]), "oppositeDirection" : true, "depth" : 3.2 * mm});
        }
        {
            var Q0;
            Q0=qCreatedBy(makeId("Front.planeOp"),FACE);
            var sketch = newSketch(context, id + "F49", { "sketchPlane" : qUnion([Q0])});
            skLineSegment(sketch, "E39.0", {"start": v(15.96, -3.2) * mm, "end": v(15.96, 0) * mm, "construction": true});
            skLineSegment(sketch, "E39.1", {"start": v(24.04, -3.2) * mm, "end": v(24.04, 0) * mm});
            skLineSegment(sketch, "E39.2", {"start": v(16.5, 0) * mm, "end": v(23.5, 0) * mm});
            skLineSegment(sketch, "E39.3", {"start": v(15.96, 0) * mm, "end": v(17.98, 0) * mm});
            skLineSegment(sketch, "E39.4", {"start": v(17.98, 0) * mm, "end": v(22.02, 0) * mm});
            skLineSegment(sketch, "E39.5", {"start": v(22.02, 0) * mm, "end": v(24.04, 0) * mm});
            skLineSegment(sketch, "E40", {"start": v(20, 0) * mm, "end": v(20, -3.2) * mm, "construction": true});
            skLineSegment(sketch, "E41", {"start": v(24.04, -1.6) * mm, "end": v(20, -1.6) * mm, "construction": true});
            skLineSegment(sketch, "E42", {"start": v(23.5, 0) * mm, "end": v(24.04, -0.31) * mm});
            skLineSegment(sketch, "E43.0.MirrorCS", {"start": v(23.5, -3.2) * mm, "end": v(24.04, -2.89) * mm});
            skLineSegment(sketch, "E44.0.MirrorCS", {"start": v(24.04, 0) * mm, "end": v(24.04, -3.2) * mm});
            skLineSegment(sketch, "E45", {"start": v(24.04, -3.2) * mm, "end": v(23.5, -3.2) * mm});
            skSolve(sketch);
        }
        {
            var Q0;
            {var subQ2=sQuery(id+"F49.wireOp",EDGE,"E43.0.MirrorCS");Q0=makeQuery(id+"F49.imprint","IMPRINT",FACE,{"disambiguationData":[TD([[makeQuery(id+"F49.imprint","IMPRINT",EDGE,{"derivedFrom":subQ2}),-1.0]])]});}
            var Q1;
            {var subQ1=sQuery(id+"F49.wireOp",EDGE,"E42");Q1=makeQuery(id+"F49.imprint","IMPRINT",FACE,{"disambiguationData":[TD([[makeQuery(id+"F49.imprint","IMPRINT",EDGE,{"derivedFrom":subQ1}),1.0]])]});}
            var Q2;
            Q2=sQuery(id+"F49.wireOp",EDGE,"E40");
            revolve(context, id + "F50", {"operationType" : NewBodyOperationType.REMOVE, "entities" : qUnion([Q0, Q1]), "axis" : qUnion([Q2]), "revolveType" : RevolveType.FULL, "oppositeDirection" : true});
        }
        {
            var Q0;
            Q0=qCreatedBy(makeId("Top.planeOp"),FACE);
            var sketch = newSketch(context, id + "F51", { "sketchPlane" : qUnion([Q0])});
            skLineSegment(sketch, "E46", {"start": v(0, 0) * mm, "end": v(0, -70) * mm, "construction": true});
            skCircle(sketch, "E47", {"center": v(0, -70) * mm, "radius": 2 * mm});
            skCircle(sketch, "E48", {"center": v(0, -70) * mm, "radius": 3.5 * mm});
            skCircle(sketch, "E49.cCircle", {"center": v(0, -70) * mm, "radius": 3.5 * mm, "construction": true});
            skLineSegment(sketch, "E49.0", {"start": v(2.02, -73.5) * mm, "end": v(-2.02, -73.5) * mm});
            skLineSegment(sketch, "E49.1", {"start": v(-2.02, -73.5) * mm, "end": v(-4.04, -70) * mm});
            skLineSegment(sketch, "E49.2", {"start": v(-4.04, -70) * mm, "end": v(-2.02, -66.5) * mm});
            skLineSegment(sketch, "E49.3", {"start": v(-2.02, -66.5) * mm, "end": v(2.02, -66.5) * mm});
            skLineSegment(sketch, "E49.4", {"start": v(2.02, -66.5) * mm, "end": v(4.04, -70) * mm});
            skLineSegment(sketch, "E49.5", {"start": v(4.04, -70) * mm, "end": v(2.02, -73.5) * mm});
            skPoint(sketch, "E49.0.midPoint", {"position": v(0, -73.5) * mm});
            skSolve(sketch);
        }
        {
            var Q0;
            Q0=makeQuery(id+"F51.imprint","IMPRINT",FACE,{"disambiguationData":[TD([[makeQuery(id+"F51.imprint","IMPRINT",EDGE,{"derivedFrom":sQuery(id+"F51.wireOp",EDGE,"E47")}),1.0]])]});
            extrude(context, id + "F52", {"entities" : qUnion([Q0]), "oppositeDirection" : true, "depth" : (18 + 3) * mm});
        }
        {
            var Q0;
            Q0=makeQuery(id+"F51.imprint","IMPRINT",FACE,{"disambiguationData":[TD([[makeQuery(id+"F51.imprint","IMPRINT",EDGE,{"derivedFrom":sQuery(id+"F51.wireOp",EDGE,"E47")}),-1.0]])]});
            var Q1;
            {var subQ0=sQuery(id+"F51.wireOp",EDGE,"E49.2");var subQ1=sQuery(id+"F51.wireOp",EDGE,"E48");var subQ2=makeQuery(id+"F51.imprint","INTERSECT",VERTEX,{"derivedFrom":[subQ1,subQ0]});Q1=makeQuery(id+"F51.imprint","IMPRINT",FACE,{"disambiguationData":[TD([[makeQuery(id+"F51.imprint","IMPRINT",EDGE,{"disambiguationData":[TD([[subQ2,-1.0]])],"derivedFrom":subQ1}),-1.0]])]});}
            var Q2;
            {var subQ0=sQuery(id+"F51.wireOp",EDGE,"E49.3");var subQ1=sQuery(id+"F51.wireOp",EDGE,"E48");var subQ2=makeQuery(id+"F51.imprint","INTERSECT",VERTEX,{"derivedFrom":[subQ1,subQ0]});Q2=makeQuery(id+"F51.imprint","IMPRINT",FACE,{"disambiguationData":[TD([[makeQuery(id+"F51.imprint","IMPRINT",EDGE,{"disambiguationData":[TD([[subQ2,-1.0]])],"derivedFrom":subQ1}),-1.0]])]});}
            var Q3;
            {var subQ1=sQuery(id+"F51.wireOp",EDGE,"E48");var subQ3=sQuery(id+"F51.wireOp",EDGE,"E49.3");var subQ5=makeQuery(id+"F51.imprint","INTERSECT",VERTEX,{"derivedFrom":[subQ1,subQ3]});Q3=makeQuery(id+"F51.imprint","IMPRINT",FACE,{"disambiguationData":[TD([[makeQuery(id+"F51.imprint","IMPRINT",EDGE,{"disambiguationData":[TD([[subQ5,1.0]])],"derivedFrom":subQ1}),-1.0]])]});}
            var Q4;
            {var subQ1=sQuery(id+"F51.wireOp",EDGE,"E48");var subQ3=sQuery(id+"F51.wireOp",EDGE,"E49.4");var subQ5=makeQuery(id+"F51.imprint","INTERSECT",VERTEX,{"derivedFrom":[subQ1,subQ3]});Q4=makeQuery(id+"F51.imprint","IMPRINT",FACE,{"disambiguationData":[TD([[makeQuery(id+"F51.imprint","IMPRINT",EDGE,{"disambiguationData":[TD([[subQ5,1.0]])],"derivedFrom":subQ1}),-1.0]])]});}
            var Q5;
            {var subQ1=sQuery(id+"F51.wireOp",EDGE,"E48");var subQ3=sQuery(id+"F51.wireOp",EDGE,"E49.0");var subQ5=makeQuery(id+"F51.imprint","INTERSECT",VERTEX,{"derivedFrom":[subQ1,subQ3]});Q5=makeQuery(id+"F51.imprint","IMPRINT",FACE,{"disambiguationData":[TD([[makeQuery(id+"F51.imprint","IMPRINT",EDGE,{"disambiguationData":[TD([[subQ5,-1.0]])],"derivedFrom":subQ1}),-1.0]])]});}
            var Q6;
            {var subQ0=sQuery(id+"F51.wireOp",EDGE,"E49.1");var subQ1=sQuery(id+"F51.wireOp",EDGE,"E48");var subQ2=makeQuery(id+"F51.imprint","INTERSECT",VERTEX,{"derivedFrom":[subQ1,subQ0]});Q6=makeQuery(id+"F51.imprint","IMPRINT",FACE,{"disambiguationData":[TD([[makeQuery(id+"F51.imprint","IMPRINT",EDGE,{"disambiguationData":[TD([[subQ2,-1.0]])],"derivedFrom":subQ1}),-1.0]])]});}
            extrude(context, id + "F53", {"entities" : qUnion([Q0, Q1, Q2, Q3, Q4, Q5, Q6]), "operationType" : NewBodyOperationType.ADD, "oppositeDirection" : true, "depth" : 3 * mm});
        }
        {
            var Q0;
            Q0=qCreatedBy(makeId("Right.planeOp"),FACE);
            var sketch = newSketch(context, id + "F54", { "sketchPlane" : qUnion([Q0])});
            skLineSegment(sketch, "E50.0", {"start": v(-73.5, 0) * mm, "end": v(-66.5, 0) * mm});
            skLineSegment(sketch, "E50.1", {"start": v(-70, -3) * mm, "end": v(-66.5, -3) * mm});
            skLineSegment(sketch, "E50.2", {"start": v(-73.5, -3) * mm, "end": v(-70, -3) * mm});
            skLineSegment(sketch, "E51", {"start": v(-70, 0) * mm, "end": v(-70, -3) * mm, "construction": true});
            skLineSegment(sketch, "E52", {"start": v(-70, -1.5) * mm, "end": v(-66.5, -1.5) * mm, "construction": true});
            skLineSegment(sketch, "E53", {"start": v(-66.5, 0) * mm, "end": v(-64.6, 0) * mm});
            skLineSegment(sketch, "E54", {"start": v(-64.6, 0) * mm, "end": v(-64.6, -1.1) * mm});
            skLineSegment(sketch, "E55", {"start": v(-64.6, -1.1) * mm, "end": v(-66.5, 0) * mm});
            skLineSegment(sketch, "E56.0.MirrorCS", {"start": v(-64.6, -1.9) * mm, "end": v(-66.5, -3) * mm});
            skLineSegment(sketch, "E57.0.MirrorCS", {"start": v(-66.5, -3) * mm, "end": v(-64.6, -3) * mm});
            skLineSegment(sketch, "E58.0.MirrorCS", {"start": v(-64.6, -3) * mm, "end": v(-64.6, -1.9) * mm});
            skSolve(sketch);
        }
        {
            var Q0;
            Q0=makeQuery(id+"F54.imprint","IMPRINT",FACE,{"disambiguationData":[TD([[makeQuery(id+"F54.imprint","IMPRINT",EDGE,{"derivedFrom":sQuery(id+"F54.wireOp",EDGE,"E53")}),-1.0]])]});
            var Q1;
            Q1=sQuery(id+"F54.wireOp",EDGE,"E51");
            revolve(context, id + "F55", {"operationType" : NewBodyOperationType.REMOVE, "entities" : qUnion([Q0]), "axis" : qUnion([Q1]), "revolveType" : RevolveType.FULL, "oppositeDirection" : true});
        }
        {
            var Q0;
            Q0=qCreatedBy(makeId("Top.planeOp"),FACE);
            var sketch = newSketch(context, id + "F56", { "sketchPlane" : qUnion([Q0])});
            skCircle(sketch, "E59.0", {"center": v(0, -70) * mm, "radius": 2 * mm, "construction": true});
            skLineSegment(sketch, "E60", {"start": v(0, -70) * mm, "end": v(0, -80) * mm, "construction": true});
            skCircle(sketch, "E61", {"center": v(0, -80) * mm, "radius": 2.5 * mm});
            skCircle(sketch, "E62", {"center": v(0, -80) * mm, "radius": 4 * mm});
            skCircle(sketch, "E63.cCircle", {"center": v(0, -80) * mm, "radius": 4 * mm, "construction": true});
            skLineSegment(sketch, "E63.0", {"start": v(2.3, -84) * mm, "end": v(-2.3, -84) * mm});
            skLineSegment(sketch, "E63.1", {"start": v(-2.3, -84) * mm, "end": v(-4.62, -80) * mm});
            skLineSegment(sketch, "E63.2", {"start": v(-4.62, -80) * mm, "end": v(-2.3, -76) * mm});
            skLineSegment(sketch, "E63.3", {"start": v(-2.3, -76) * mm, "end": v(2.3, -76) * mm});
            skLineSegment(sketch, "E63.4", {"start": v(2.3, -76) * mm, "end": v(4.62, -80) * mm});
            skLineSegment(sketch, "E63.5", {"start": v(4.62, -80) * mm, "end": v(2.3, -84) * mm});
            skPoint(sketch, "E63.0.midPoint", {"position": v(0, -84) * mm});
            skSolve(sketch);
        }
        {
            var Q0;
            Q0=makeQuery(id+"F56.imprint","IMPRINT",FACE,{"disambiguationData":[TD([[makeQuery(id+"F56.imprint","IMPRINT",EDGE,{"derivedFrom":sQuery(id+"F56.wireOp",EDGE,"E61")}),1.0]])]});
            extrude(context, id + "F57", {"entities" : qUnion([Q0]), "oppositeDirection" : true, "depth" : (25 + 3.7) * mm});
        }
        {
            var Q0;
            Q0=makeQuery(id+"F56.imprint","IMPRINT",FACE,{"disambiguationData":[TD([[makeQuery(id+"F56.imprint","IMPRINT",EDGE,{"derivedFrom":sQuery(id+"F56.wireOp",EDGE,"E61")}),-1.0]])]});
            var Q1;
            {var subQ0=sQuery(id+"F56.wireOp",EDGE,"E63.3");var subQ1=sQuery(id+"F56.wireOp",EDGE,"E62");var subQ2=makeQuery(id+"F56.imprint","INTERSECT",VERTEX,{"derivedFrom":[subQ1,subQ0]});Q1=makeQuery(id+"F56.imprint","IMPRINT",FACE,{"disambiguationData":[TD([[makeQuery(id+"F56.imprint","IMPRINT",EDGE,{"disambiguationData":[TD([[subQ2,-1.0]])],"derivedFrom":subQ1}),-1.0]])]});}
            var Q2;
            {var subQ0=sQuery(id+"F56.wireOp",EDGE,"E63.3");var subQ1=sQuery(id+"F56.wireOp",EDGE,"E62");var subQ2=makeQuery(id+"F56.imprint","INTERSECT",VERTEX,{"derivedFrom":[subQ1,subQ0]});Q2=makeQuery(id+"F56.imprint","IMPRINT",FACE,{"disambiguationData":[TD([[makeQuery(id+"F56.imprint","IMPRINT",EDGE,{"disambiguationData":[TD([[subQ2,1.0]])],"derivedFrom":subQ1}),-1.0]])]});}
            var Q3;
            {var subQ0=sQuery(id+"F56.wireOp",EDGE,"E63.2");var subQ1=sQuery(id+"F56.wireOp",EDGE,"E62");var subQ2=makeQuery(id+"F56.imprint","INTERSECT",VERTEX,{"derivedFrom":[subQ1,subQ0]});Q3=makeQuery(id+"F56.imprint","IMPRINT",FACE,{"disambiguationData":[TD([[makeQuery(id+"F56.imprint","IMPRINT",EDGE,{"disambiguationData":[TD([[subQ2,-1.0]])],"derivedFrom":subQ1}),-1.0]])]});}
            var Q4;
            {var subQ0=sQuery(id+"F56.wireOp",EDGE,"E63.1");var subQ1=sQuery(id+"F56.wireOp",EDGE,"E62");var subQ2=makeQuery(id+"F56.imprint","INTERSECT",VERTEX,{"derivedFrom":[subQ1,subQ0]});Q4=makeQuery(id+"F56.imprint","IMPRINT",FACE,{"disambiguationData":[TD([[makeQuery(id+"F56.imprint","IMPRINT",EDGE,{"disambiguationData":[TD([[subQ2,-1.0]])],"derivedFrom":subQ1}),-1.0]])]});}
            var Q5;
            {var subQ1=sQuery(id+"F56.wireOp",EDGE,"E62");var subQ3=sQuery(id+"F56.wireOp",EDGE,"E63.0");var subQ5=makeQuery(id+"F56.imprint","INTERSECT",VERTEX,{"derivedFrom":[subQ1,subQ3]});Q5=makeQuery(id+"F56.imprint","IMPRINT",FACE,{"disambiguationData":[TD([[makeQuery(id+"F56.imprint","IMPRINT",EDGE,{"disambiguationData":[TD([[subQ5,-1.0]])],"derivedFrom":subQ1}),-1.0]])]});}
            var Q6;
            {var subQ1=sQuery(id+"F56.wireOp",EDGE,"E62");var subQ3=sQuery(id+"F56.wireOp",EDGE,"E63.4");var subQ5=makeQuery(id+"F56.imprint","INTERSECT",VERTEX,{"derivedFrom":[subQ1,subQ3]});Q6=makeQuery(id+"F56.imprint","IMPRINT",FACE,{"disambiguationData":[TD([[makeQuery(id+"F56.imprint","IMPRINT",EDGE,{"disambiguationData":[TD([[subQ5,1.0]])],"derivedFrom":subQ1}),-1.0]])]});}
            extrude(context, id + "F58", {"entities" : qUnion([Q0, Q1, Q2, Q3, Q4, Q5, Q6]), "operationType" : NewBodyOperationType.ADD, "oppositeDirection" : true, "depth" : 3.7 * mm});
        }
        {
            var Q0;
            Q0=qCreatedBy(makeId("Right.planeOp"),FACE);
            var sketch = newSketch(context, id + "F59", { "sketchPlane" : qUnion([Q0])});
            skLineSegment(sketch, "E64.0", {"start": v(-84, 0) * mm, "end": v(-76, 0) * mm});
            skLineSegment(sketch, "E65", {"start": v(-80, 0) * mm, "end": v(-80, -2.78) * mm, "construction": true});
            skLineSegment(sketch, "E66", {"start": v(-84, 0) * mm, "end": v(-86.4, 0) * mm});
            skLineSegment(sketch, "E67", {"start": v(-86.4, 0) * mm, "end": v(-86.4, -1.38) * mm});
            skLineSegment(sketch, "E68", {"start": v(-86.4, -1.38) * mm, "end": v(-84, 0) * mm});
            skSolve(sketch);
        }
        {
            var Q0;
            Q0=makeQuery(id+"F59.imprint","IMPRINT",FACE,{"disambiguationData":[TD([[makeQuery(id+"F59.imprint","IMPRINT",EDGE,{"derivedFrom":sQuery(id+"F59.wireOp",EDGE,"E66")}),1.0]])]});
            var Q1;
            Q1=sQuery(id+"F59.wireOp",EDGE,"E65");
            revolve(context, id + "F60", {"operationType" : NewBodyOperationType.REMOVE, "entities" : qUnion([Q0]), "axis" : qUnion([Q1]), "revolveType" : RevolveType.FULL, "oppositeDirection" : true});
        }
        {
            var Q0;
            Q0=makeQuery(id+"F57.opExtrude","SWEPT_BODY",BODY,{"disambiguationData":[OSD([sQuery(id+"F56.wireOp",EDGE,"E61")])]});
            transform(context, id + "F61", {"entities" : qUnion([Q0]), "transformType" : TransformType.TRANSLATION_3D, "dx" : 10 * mm, "dy" : 0 * mm, "dz" : 0 * mm, "makeCopy" : true});
        }
        {
            var Q0;
            Q0=makeQuery(id+"F61.opPattern","COPY",FACE,{"derivedFrom":makeQuery(id+"F57.opExtrude","CAP_FACE",FACE,{"disambiguationData":[OSD([sQuery(id+"F56.wireOp",EDGE,"E61")])],"isStart":false}),"instanceName":"1"});
            extrude(context, id + "F62", {"entities" : qUnion([Q0]), "operationType" : NewBodyOperationType.ADD, "depth" : 10 * mm});
        }
        {
            var Q0;
            Q0=qCreatedBy(makeId("Top.planeOp"),FACE);
            var sketch = newSketch(context, id + "F63", { "sketchPlane" : qUnion([Q0])});
            skLineSegment(sketch, "E69", {"start": v(0, -50) * mm, "end": v(20, -50) * mm, "construction": true});
            skCircle(sketch, "E70", {"center": v(20, -50) * mm, "radius": 1.5 * mm});
            skCircle(sketch, "E71", {"center": v(20, -50) * mm, "radius": 3 * mm});
            skCircle(sketch, "E72", {"center": v(20, -50) * mm, "radius": 3.36 * mm});
            skCircle(sketch, "E73.cCircle", {"center": v(20, -50) * mm, "radius": 1 * mm, "construction": true});
            skLineSegment(sketch, "E73.0", {"start": v(20.58, -51) * mm, "end": v(19.42, -51) * mm});
            skLineSegment(sketch, "E73.1", {"start": v(19.42, -51) * mm, "end": v(18.85, -50) * mm});
            skLineSegment(sketch, "E73.2", {"start": v(18.85, -50) * mm, "end": v(19.42, -49) * mm});
            skLineSegment(sketch, "E73.3", {"start": v(19.42, -49) * mm, "end": v(20.58, -49) * mm});
            skLineSegment(sketch, "E73.4", {"start": v(20.58, -49) * mm, "end": v(21.15, -50) * mm});
            skLineSegment(sketch, "E73.5", {"start": v(21.15, -50) * mm, "end": v(20.58, -51) * mm});
            skPoint(sketch, "E73.0.midPoint", {"position": v(20, -51) * mm});
            skSolve(sketch);
        }
        {
            var Q0;
            Q0=makeQuery(id+"F63.imprint","IMPRINT",FACE,{"disambiguationData":[TD([[makeQuery(id+"F63.imprint","IMPRINT",EDGE,{"derivedFrom":sQuery(id+"F63.wireOp",EDGE,"E70")}),1.0]])]});
            var Q1;
            Q1=makeQuery(id+"F63.imprint","IMPRINT",FACE,{"disambiguationData":[TD([[makeQuery(id+"F63.imprint","IMPRINT",EDGE,{"derivedFrom":sQuery(id+"F63.wireOp",EDGE,"E73.0")}),-1.0]])]});
            extrude(context, id + "F64", {"entities" : qUnion([Q0, Q1]), "oppositeDirection" : true, "depth" : 12 * mm});
        }
        {
            var Q0;
            Q0=makeQuery(id+"F63.imprint","IMPRINT",FACE,{"disambiguationData":[TD([[makeQuery(id+"F63.imprint","IMPRINT",EDGE,{"derivedFrom":sQuery(id+"F63.wireOp",EDGE,"E70")}),-1.0]])]});
            var Q1;
            Q1=makeQuery(id+"F63.imprint","IMPRINT",FACE,{"disambiguationData":[TD([[makeQuery(id+"F63.imprint","IMPRINT",EDGE,{"derivedFrom":sQuery(id+"F63.wireOp",EDGE,"E71")}),-1.0]])]});
            extrude(context, id + "F65", {"entities" : qUnion([Q0, Q1]), "operationType" : NewBodyOperationType.ADD, "oppositeDirection" : true, "depth" : 1.86 * mm});
        }
        {
            var Q0;
            Q0=makeQuery(id+"F65.opExtrude","CAP_EDGE",EDGE,{"disambiguationData":[OSD([sQuery(id+"F63.wireOp",EDGE,"E72")])],"isStart":false});
            chamfer(context, id + "F66", {"entities" : qUnion([Q0]), "width" : 1.85 * mm, "tangentPropagation" : true});
        }
        {
            var Q0;
            Q0=makeQuery(id+"F63.imprint","IMPRINT",FACE,{"disambiguationData":[TD([[makeQuery(id+"F63.imprint","IMPRINT",EDGE,{"derivedFrom":sQuery(id+"F63.wireOp",EDGE,"E71")}),-1.0]])]});
            extrude(context, id + "F67", {"entities" : qUnion([Q0]), "operationType" : NewBodyOperationType.REMOVE, "oppositeDirection" : true, "depth" : 1 * mm});
        }
        {
            var Q0;
            Q0=makeQuery(id+"F63.imprint","IMPRINT",FACE,{"disambiguationData":[TD([[makeQuery(id+"F63.imprint","IMPRINT",EDGE,{"derivedFrom":sQuery(id+"F63.wireOp",EDGE,"E73.0")}),-1.0]])]});
            extrude(context, id + "F68", {"entities" : qUnion([Q0]), "operationType" : NewBodyOperationType.REMOVE, "oppositeDirection" : true, "depth" : 1.05 * mm});
        }
    });
